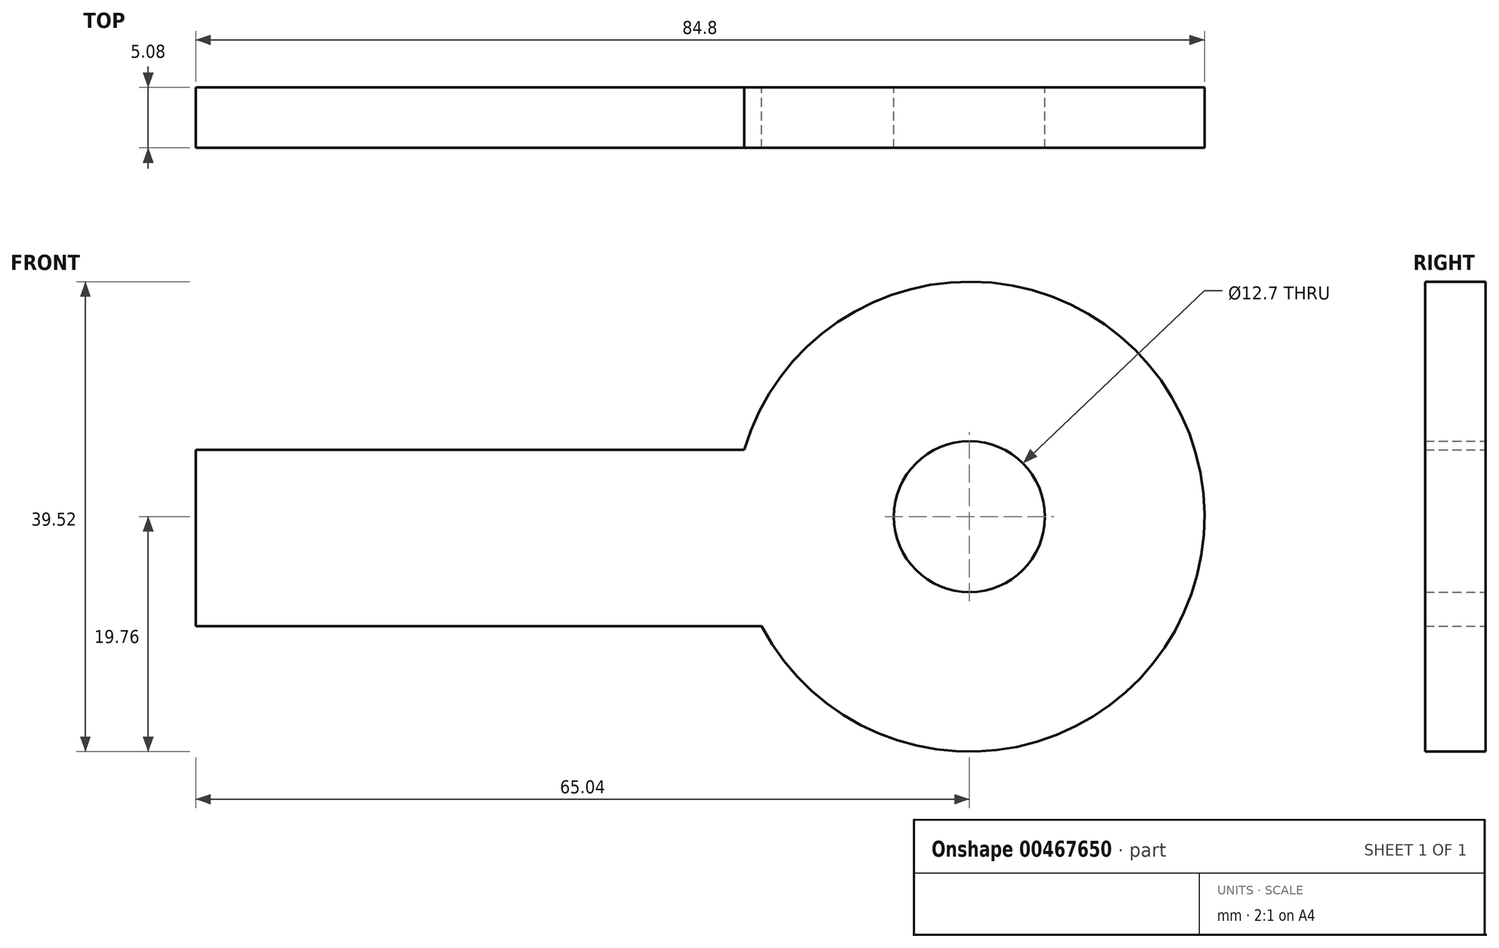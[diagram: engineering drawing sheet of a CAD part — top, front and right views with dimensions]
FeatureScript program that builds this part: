
annotation { "Feature Type Name" : "Feature", "Feature Type Description" : "" }
export const myFeature = defineFeature(function(context is Context, id is Id, definition is map)
    precondition{}
    {
        {
            var Q0;
            Q0=qCreatedBy(makeId("Front.planeOp"),FACE);
            var sketch = newSketch(context, id + "F0", { "sketchPlane" : qUnion([Q0])});
            skCircle(sketch, "E0", {"center": v(0, 0) * mm, "radius": 19.76 * mm});
            skCircle(sketch, "E1", {"center": v(0, 0) * mm, "radius": 6.35 * mm});
            skLineSegment(sketch, "E2", {"start": v(-18.95, 5.62) * mm, "end": v(-65.04, 5.62) * mm});
            skLineSegment(sketch, "E3", {"start": v(-65.04, 5.62) * mm, "end": v(-65.04, -9.2) * mm});
            skLineSegment(sketch, "E4", {"start": v(-65.04, -9.2) * mm, "end": v(-17.48, -9.2) * mm});
            skSolve(sketch);
        }
        {
            var Q0;
            Q0 = qSketchRegion(id + "F0", true);
            extrude(context, id + "F1", {"entities" : qUnion([Q0]), "depth" : 5.08 * mm});
        }
    });
